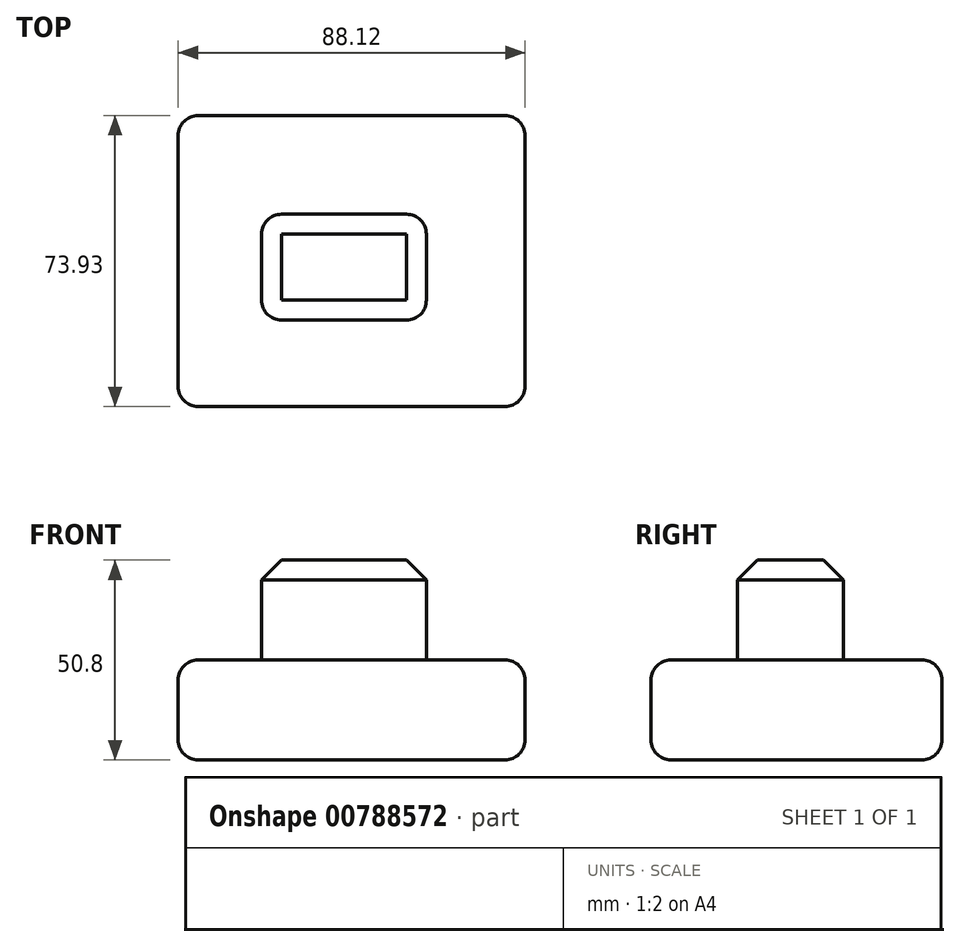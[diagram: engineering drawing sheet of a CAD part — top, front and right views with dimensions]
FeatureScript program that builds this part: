
annotation { "Feature Type Name" : "Feature", "Feature Type Description" : "" }
export const myFeature = defineFeature(function(context is Context, id is Id, definition is map)
    precondition{}
    {
        {
            var Q0;
            Q0=qCreatedBy(makeId("Top.planeOp"),FACE);
            var sketch = newSketch(context, id + "F0", { "sketchPlane" : qUnion([Q0])});
            skLineSegment(sketch, "E0.bottom", {"start": v(-42.5, 40.1) * mm, "end": v(45.63, 40.1) * mm});
            skLineSegment(sketch, "E0.top", {"start": v(-42.5, -33.83) * mm, "end": v(45.63, -33.83) * mm});
            skLineSegment(sketch, "E0.left", {"start": v(-42.5, 40.1) * mm, "end": v(-42.5, -33.83) * mm});
            skLineSegment(sketch, "E0.right", {"start": v(45.63, 40.1) * mm, "end": v(45.63, -33.83) * mm});
            skSolve(sketch);
        }
        {
            var Q0;
            Q0=makeQuery(id+"F0.imprint","IMPRINT",FACE,{"disambiguationData":[TD([[makeQuery(id+"F0.imprint","IMPRINT",EDGE,{"derivedFrom":sQuery(id+"F0.wireOp",EDGE,"E0.bottom")}),-1.0]])]});
            extrude(context, id + "F1", {"entities" : qUnion([Q0]), "depth" : 25.4 * mm, "offsetDistance" : 25.4 * mm});
        }
        {
            var Q0;
            Q0=makeQuery(id+"F1.opExtrude","CAP_EDGE",EDGE,{"disambiguationData":[OSD([sQuery(id+"F0.wireOp",EDGE,"E0.top")])],"isStart":true});
            var Q1;
            Q1=makeQuery(id+"F1.opExtrude","CAP_EDGE",EDGE,{"disambiguationData":[OSD([sQuery(id+"F0.wireOp",EDGE,"E0.left")])],"isStart":true});
            var Q2;
            Q2=makeQuery(id+"F1.opExtrude","CAP_EDGE",EDGE,{"disambiguationData":[OSD([sQuery(id+"F0.wireOp",EDGE,"E0.bottom")])],"isStart":true});
            var Q3;
            Q3=makeQuery(id+"F1.opExtrude","CAP_EDGE",EDGE,{"disambiguationData":[OSD([sQuery(id+"F0.wireOp",EDGE,"E0.right")])],"isStart":true});
            var Q4;
            Q4=makeQuery(id+"F1.opExtrude","CAP_EDGE",EDGE,{"disambiguationData":[OSD([sQuery(id+"F0.wireOp",EDGE,"E0.left")])],"isStart":false});
            var Q5;
            Q5=makeQuery(id+"F1.opExtrude","CAP_EDGE",EDGE,{"disambiguationData":[OSD([sQuery(id+"F0.wireOp",EDGE,"E0.top")])],"isStart":false});
            var Q6;
            Q6=makeQuery(id+"F1.opExtrude","CAP_EDGE",EDGE,{"disambiguationData":[OSD([sQuery(id+"F0.wireOp",EDGE,"E0.right")])],"isStart":false});
            var Q7;
            Q7=makeQuery(id+"F1.opExtrude","CAP_EDGE",EDGE,{"disambiguationData":[OSD([sQuery(id+"F0.wireOp",EDGE,"E0.bottom")])],"isStart":false});
            fillet(context, id + "F2", {"entities" : qUnion([Q0, Q1, Q2, Q3, Q4, Q5, Q6, Q7]), "radius" : 5.08 * mm, "tangentPropagation" : true, "allowEdgeOverflow" : false});
        }
        {
            var Q0;
            Q0=makeQuery(id+"F1.opExtrude","CAP_FACE",FACE,{"disambiguationData":[OSD([sQuery(id+"F0.wireOp",EDGE,"E0.bottom"),sQuery(id+"F0.wireOp",EDGE,"E0.top"),sQuery(id+"F0.wireOp",EDGE,"E0.left"),sQuery(id+"F0.wireOp",EDGE,"E0.right")])],"isStart":false});
            var sketch = newSketch(context, id + "F3", { "sketchPlane" : qUnion([Q0])});
            skLineSegment(sketch, "E1.bottom", {"start": v(-21.3, 15.02) * mm, "end": v(20.56, 15.02) * mm});
            skLineSegment(sketch, "E1.top", {"start": v(-21.3, -11.9) * mm, "end": v(20.56, -11.9) * mm});
            skLineSegment(sketch, "E1.left", {"start": v(-21.3, 15.02) * mm, "end": v(-21.3, -11.9) * mm});
            skLineSegment(sketch, "E1.right", {"start": v(20.56, 15.02) * mm, "end": v(20.56, -11.9) * mm});
            skSolve(sketch);
        }
        {
            var Q0;
            Q0=makeQuery(id+"F3.imprint","IMPRINT",FACE,{"disambiguationData":[TD([[makeQuery(id+"F3.imprint","IMPRINT",EDGE,{"derivedFrom":sQuery(id+"F3.wireOp",EDGE,"E1.bottom")}),-1.0]])]});
            extrude(context, id + "F4", {"entities" : qUnion([Q0]), "operationType" : NewBodyOperationType.ADD, "depth" : 25.4 * mm, "offsetDistance" : 25.4 * mm});
        }
        {
            var Q0;
            Q0=makeQuery(id+"F4.opExtrude","CAP_EDGE",EDGE,{"disambiguationData":[OSD([sQuery(id+"F3.wireOp",EDGE,"E1.top")])],"isStart":true});
            var Q1;
            Q1=makeQuery(id+"F4.opExtrude","CAP_EDGE",EDGE,{"disambiguationData":[OSD([sQuery(id+"F3.wireOp",EDGE,"E1.right")])],"isStart":true});
            var Q2;
            Q2=makeQuery(id+"F4.opExtrude","CAP_EDGE",EDGE,{"disambiguationData":[OSD([sQuery(id+"F3.wireOp",EDGE,"E1.left")])],"isStart":true});
            var Q3;
            Q3=makeQuery(id+"F4.opExtrude","CAP_EDGE",EDGE,{"disambiguationData":[OSD([sQuery(id+"F3.wireOp",EDGE,"E1.bottom")])],"isStart":true});
            var Q4;
            Q4=makeQuery(id+"F4.opExtrude","SWEPT_EDGE",EDGE,{"disambiguationData":[OSD([sQuery(id+"F3.wireOp",EDGE,"E1.bottom"),sQuery(id+"F3.wireOp",EDGE,"E1.left")])]});
            var Q5;
            Q5=makeQuery(id+"F4.opExtrude","SWEPT_EDGE",EDGE,{"disambiguationData":[OSD([sQuery(id+"F3.wireOp",EDGE,"E1.top"),sQuery(id+"F3.wireOp",EDGE,"E1.left")])]});
            var Q6;
            Q6=makeQuery(id+"F4.opExtrude","SWEPT_EDGE",EDGE,{"disambiguationData":[OSD([sQuery(id+"F3.wireOp",EDGE,"E1.top"),sQuery(id+"F3.wireOp",EDGE,"E1.right")])]});
            var Q7;
            Q7=makeQuery(id+"F4.opExtrude","SWEPT_EDGE",EDGE,{"disambiguationData":[OSD([sQuery(id+"F3.wireOp",EDGE,"E1.bottom"),sQuery(id+"F3.wireOp",EDGE,"E1.right")])]});
            fillet(context, id + "F5", {"entities" : qUnion([Q0, Q1, Q2, Q3, Q4, Q5, Q6, Q7]), "radius" : 5.08 * mm, "tangentPropagation" : true, "allowEdgeOverflow" : false});
        }
        {
            var Q0;
            Q0=makeQuery(id+"F4.opExtrude","CAP_EDGE",EDGE,{"disambiguationData":[OSD([sQuery(id+"F3.wireOp",EDGE,"E1.top")])],"isStart":false});
            chamfer(context, id + "F6", {"entities" : qUnion([Q0]), "width" : 5.08 * mm, "tangentPropagation" : true});
        }
        {
            var Q0;
            Q0=makeQuery(id+"F1.opExtrude","SWEPT_EDGE",EDGE,{"disambiguationData":[OSD([sQuery(id+"F0.wireOp",EDGE,"E0.top"),sQuery(id+"F0.wireOp",EDGE,"E0.left")])]});
            var Q1;
            Q1=makeQuery(id+"F1.opExtrude","SWEPT_EDGE",EDGE,{"disambiguationData":[OSD([sQuery(id+"F0.wireOp",EDGE,"E0.bottom"),sQuery(id+"F0.wireOp",EDGE,"E0.left")])]});
            var Q2;
            Q2=makeQuery(id+"F1.opExtrude","SWEPT_EDGE",EDGE,{"disambiguationData":[OSD([sQuery(id+"F0.wireOp",EDGE,"E0.bottom"),sQuery(id+"F0.wireOp",EDGE,"E0.right")])]});
            var Q3;
            Q3=makeQuery(id+"F1.opExtrude","SWEPT_EDGE",EDGE,{"disambiguationData":[OSD([sQuery(id+"F0.wireOp",EDGE,"E0.top"),sQuery(id+"F0.wireOp",EDGE,"E0.right")])]});
            fillet(context, id + "F7", {"entities" : qUnion([Q0, Q1, Q2, Q3]), "radius" : 5.08 * mm, "tangentPropagation" : true, "allowEdgeOverflow" : false});
        }
    });
